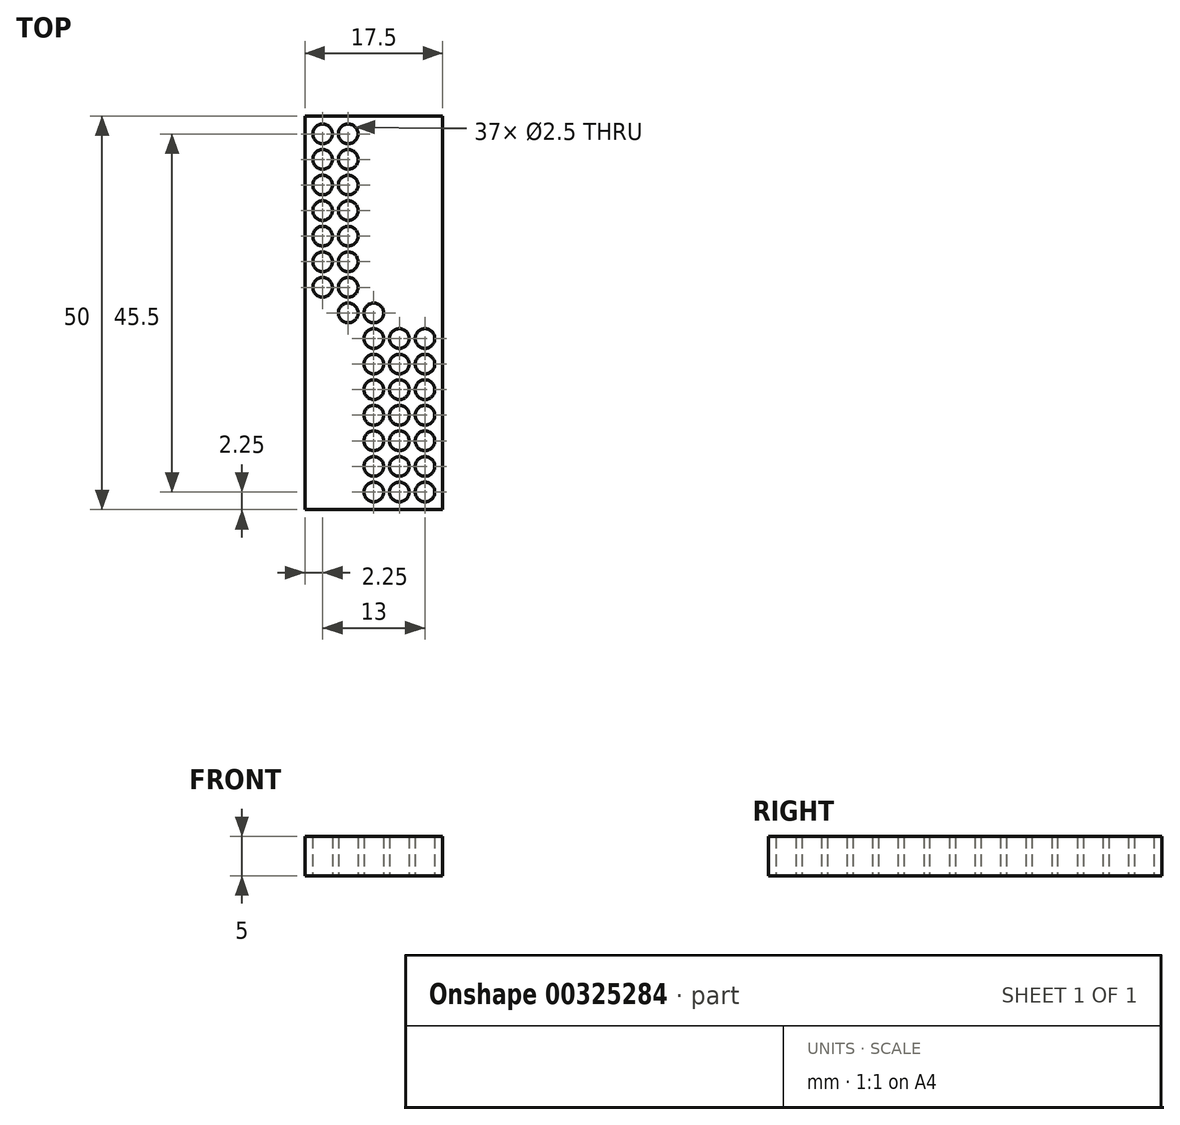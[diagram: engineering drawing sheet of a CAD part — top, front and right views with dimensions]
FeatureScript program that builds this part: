
annotation { "Feature Type Name" : "Feature", "Feature Type Description" : "" }
export const myFeature = defineFeature(function(context is Context, id is Id, definition is map)
    precondition{}
    {
        {
            var Q0;
            Q0=qCreatedBy(makeId("Top.planeOp"),FACE);
            var sketch = newSketch(context, id + "F0", { "sketchPlane" : qUnion([Q0])});
            skLineSegment(sketch, "E0.bottom", {"start": v(8.75, -25) * mm, "end": v(-8.75, -25) * mm});
            skLineSegment(sketch, "E0.top", {"start": v(8.75, 25) * mm, "end": v(-8.75, 25) * mm});
            skLineSegment(sketch, "E0.left", {"start": v(8.75, -25) * mm, "end": v(8.75, 25) * mm});
            skLineSegment(sketch, "E0.right", {"start": v(-8.75, -25) * mm, "end": v(-8.75, 25) * mm});
            skPoint(sketch, "E0.middle", {"position": v(0, 0) * mm});
            skCircle(sketch, "E1", {"center": v(0, 0) * mm, "radius": 1.25 * mm});
            skCircle(sketch, "E2.0.1.0", {"center": v(0, 3.25) * mm, "radius": 1.25 * mm});
            skCircle(sketch, "E2.0.2.0", {"center": v(0, 6.5) * mm, "radius": 1.25 * mm});
            skCircle(sketch, "E2.0.3.0", {"center": v(0, 9.75) * mm, "radius": 1.25 * mm});
            skCircle(sketch, "E2.0.4.0", {"center": v(0, 13) * mm, "radius": 1.25 * mm});
            skCircle(sketch, "E2.0.5.0", {"center": v(0, 16.25) * mm, "radius": 1.25 * mm});
            skCircle(sketch, "E2.0.6.0", {"center": v(0, 19.5) * mm, "radius": 1.25 * mm});
            skCircle(sketch, "E2.0.7.0", {"center": v(0, 22.75) * mm, "radius": 1.25 * mm});
            skCircle(sketch, "E2.1.0.0", {"center": v(3.25, 0) * mm, "radius": 1.25 * mm});
            skCircle(sketch, "E2.1.1.0", {"center": v(3.25, 3.25) * mm, "radius": 1.25 * mm});
            skCircle(sketch, "E2.1.2.0", {"center": v(3.25, 6.5) * mm, "radius": 1.25 * mm});
            skCircle(sketch, "E2.1.3.0", {"center": v(3.25, 9.75) * mm, "radius": 1.25 * mm});
            skCircle(sketch, "E2.1.4.0", {"center": v(3.25, 13) * mm, "radius": 1.25 * mm});
            skCircle(sketch, "E2.1.5.0", {"center": v(3.25, 16.25) * mm, "radius": 1.25 * mm});
            skCircle(sketch, "E2.1.6.0", {"center": v(3.25, 19.5) * mm, "radius": 1.25 * mm});
            skCircle(sketch, "E2.1.7.0", {"center": v(3.25, 22.75) * mm, "radius": 1.25 * mm});
            skCircle(sketch, "E2.2.0.0", {"center": v(6.5, 0) * mm, "radius": 1.25 * mm});
            skCircle(sketch, "E2.2.1.0", {"center": v(6.5, 3.25) * mm, "radius": 1.25 * mm});
            skCircle(sketch, "E2.2.2.0", {"center": v(6.5, 6.5) * mm, "radius": 1.25 * mm});
            skCircle(sketch, "E2.2.3.0", {"center": v(6.5, 9.75) * mm, "radius": 1.25 * mm});
            skCircle(sketch, "E2.2.4.0", {"center": v(6.5, 13) * mm, "radius": 1.25 * mm});
            skCircle(sketch, "E2.2.5.0", {"center": v(6.5, 16.25) * mm, "radius": 1.25 * mm});
            skCircle(sketch, "E2.2.6.0", {"center": v(6.5, 19.5) * mm, "radius": 1.25 * mm});
            skCircle(sketch, "E2.2.7.0", {"center": v(6.5, 22.75) * mm, "radius": 1.25 * mm});
            skLineSegment(sketch, "E2.direction1", {"start": v(0, 0) * mm, "end": v(3.25, 0) * mm, "construction": true});
            skLineSegment(sketch, "E2.direction2", {"start": v(0, 0) * mm, "end": v(0, 3.25) * mm, "construction": true});
            skCircle(sketch, "E3.MirrorC", {"center": v(-3.25, 19.5) * mm, "radius": 1.25 * mm});
            skCircle(sketch, "E4.MirrorC", {"center": v(-6.5, 9.75) * mm, "radius": 1.25 * mm});
            skCircle(sketch, "E5.MirrorC", {"center": v(-6.5, 6.5) * mm, "radius": 1.25 * mm});
            skCircle(sketch, "E6.MirrorC", {"center": v(-6.5, 16.25) * mm, "radius": 1.25 * mm});
            skCircle(sketch, "E7.MirrorC", {"center": v(-6.5, 3.25) * mm, "radius": 1.25 * mm});
            skCircle(sketch, "E8.MirrorC", {"center": v(-6.5, 22.75) * mm, "radius": 1.25 * mm});
            skCircle(sketch, "E9.MirrorC", {"center": v(-6.5, 13) * mm, "radius": 1.25 * mm});
            skCircle(sketch, "E10.MirrorC", {"center": v(-3.25, 13) * mm, "radius": 1.25 * mm});
            skCircle(sketch, "E11.MirrorC", {"center": v(-3.25, 9.75) * mm, "radius": 1.25 * mm});
            skCircle(sketch, "E12.MirrorC", {"center": v(-3.25, 6.5) * mm, "radius": 1.25 * mm});
            skCircle(sketch, "E13.MirrorC", {"center": v(-3.25, 16.25) * mm, "radius": 1.25 * mm});
            skCircle(sketch, "E14.MirrorC", {"center": v(-3.25, 3.25) * mm, "radius": 1.25 * mm});
            skCircle(sketch, "E15.MirrorC", {"center": v(-3.25, 22.75) * mm, "radius": 1.25 * mm});
            skCircle(sketch, "E16.MirrorC", {"center": v(-6.5, 19.5) * mm, "radius": 1.25 * mm});
            skCircle(sketch, "E17.MirrorC", {"center": v(-3.25, -22.75) * mm, "radius": 1.25 * mm});
            skCircle(sketch, "E18.MirrorC", {"center": v(-3.25, -19.5) * mm, "radius": 1.25 * mm});
            skCircle(sketch, "E19.MirrorC", {"center": v(-3.25, -9.75) * mm, "radius": 1.25 * mm});
            skCircle(sketch, "E20.MirrorC", {"center": v(-6.5, -16.25) * mm, "radius": 1.25 * mm});
            skCircle(sketch, "E21.MirrorC", {"center": v(-3.25, -6.5) * mm, "radius": 1.25 * mm});
            skCircle(sketch, "E22.MirrorC", {"center": v(-3.25, -16.25) * mm, "radius": 1.25 * mm});
            skCircle(sketch, "E23.MirrorC", {"center": v(-3.25, -3.25) * mm, "radius": 1.25 * mm});
            skCircle(sketch, "E24.MirrorC", {"center": v(-6.5, -9.75) * mm, "radius": 1.25 * mm});
            skCircle(sketch, "E25.MirrorC", {"center": v(-6.5, -19.5) * mm, "radius": 1.25 * mm});
            skCircle(sketch, "E26.MirrorC", {"center": v(-6.5, -22.75) * mm, "radius": 1.25 * mm});
            skCircle(sketch, "E27.MirrorC", {"center": v(-6.5, -13) * mm, "radius": 1.25 * mm});
            skCircle(sketch, "E28.MirrorC", {"center": v(-6.5, -6.5) * mm, "radius": 1.25 * mm});
            skCircle(sketch, "E29.MirrorC", {"center": v(-6.5, -3.25) * mm, "radius": 1.25 * mm});
            skCircle(sketch, "E30.MirrorC", {"center": v(-3.25, -13) * mm, "radius": 1.25 * mm});
            skCircle(sketch, "E31.MirrorC", {"center": v(3.25, -13) * mm, "radius": 1.25 * mm});
            skCircle(sketch, "E32.MirrorC", {"center": v(3.25, -9.75) * mm, "radius": 1.25 * mm});
            skCircle(sketch, "E33.MirrorC", {"center": v(6.5, -16.25) * mm, "radius": 1.25 * mm});
            skCircle(sketch, "E34.MirrorC", {"center": v(3.25, -6.5) * mm, "radius": 1.25 * mm});
            skCircle(sketch, "E35.MirrorC", {"center": v(3.25, -3.25) * mm, "radius": 1.25 * mm});
            skCircle(sketch, "E36.MirrorC", {"center": v(3.25, -22.75) * mm, "radius": 1.25 * mm});
            skCircle(sketch, "E37.MirrorC", {"center": v(3.25, -19.5) * mm, "radius": 1.25 * mm});
            skCircle(sketch, "E38.MirrorC", {"center": v(6.5, -6.5) * mm, "radius": 1.25 * mm});
            skCircle(sketch, "E39.MirrorC", {"center": v(6.5, -19.5) * mm, "radius": 1.25 * mm});
            skCircle(sketch, "E40.MirrorC", {"center": v(6.5, -13) * mm, "radius": 1.25 * mm});
            skCircle(sketch, "E41.MirrorC", {"center": v(6.5, -3.25) * mm, "radius": 1.25 * mm});
            skCircle(sketch, "E42.MirrorC", {"center": v(6.5, -22.75) * mm, "radius": 1.25 * mm});
            skCircle(sketch, "E43.MirrorC", {"center": v(3.25, -16.25) * mm, "radius": 1.25 * mm});
            skCircle(sketch, "E44.MirrorC", {"center": v(6.5, -9.75) * mm, "radius": 1.25 * mm});
            skCircle(sketch, "E45.MirrorC", {"center": v(0, -6.5) * mm, "radius": 1.25 * mm});
            skCircle(sketch, "E46.MirrorC", {"center": v(0, -9.75) * mm, "radius": 1.25 * mm});
            skCircle(sketch, "E47.MirrorC", {"center": v(0, -22.75) * mm, "radius": 1.25 * mm});
            skCircle(sketch, "E48.MirrorC", {"center": v(0, -19.5) * mm, "radius": 1.25 * mm});
            skCircle(sketch, "E49.MirrorC", {"center": v(0, -16.25) * mm, "radius": 1.25 * mm});
            skCircle(sketch, "E50.MirrorC", {"center": v(0, -13) * mm, "radius": 1.25 * mm});
            skCircle(sketch, "E51.MirrorC", {"center": v(0, -3.25) * mm, "radius": 1.25 * mm});
            skLineSegment(sketch, "E52.MirrorCS", {"start": v(8.75, 25) * mm, "end": v(8.75, -25) * mm});
            skCircle(sketch, "E53.MirrorC", {"center": v(-6.5, 0) * mm, "radius": 1.25 * mm});
            skCircle(sketch, "E54.MirrorC", {"center": v(-3.25, 0) * mm, "radius": 1.25 * mm});
            skSolve(sketch);
        }
        {
            var Q0;
            Q0=makeQuery(id+"F0.imprint","IMPRINT",FACE,{"disambiguationData":[TD([[makeQuery(id+"F0.imprint","IMPRINT",EDGE,{"derivedFrom":sQuery(id+"F0.wireOp",EDGE,"E0.bottom")}),-1.0]])]});
            extrude(context, id + "F1", {"entities" : qUnion([Q0]), "depth" : 1 * mm});
        }
        {
            var Q0;
            Q0=makeQuery(id+"F0.imprint","IMPRINT",FACE,{"disambiguationData":[TD([[makeQuery(id+"F0.imprint","IMPRINT",EDGE,{"derivedFrom":sQuery(id+"F0.wireOp",EDGE,"E8.MirrorC")}),-1.0]])]});
            var Q1;
            Q1=makeQuery(id+"F0.imprint","IMPRINT",FACE,{"disambiguationData":[TD([[makeQuery(id+"F0.imprint","IMPRINT",EDGE,{"derivedFrom":sQuery(id+"F0.wireOp",EDGE,"E15.MirrorC")}),-1.0]])]});
            var Q2;
            Q2=makeQuery(id+"F0.imprint","IMPRINT",FACE,{"disambiguationData":[TD([[makeQuery(id+"F0.imprint","IMPRINT",EDGE,{"derivedFrom":sQuery(id+"F0.wireOp",EDGE,"E2.0.7.0")}),1.0]])]});
            var Q3;
            Q3=makeQuery(id+"F0.imprint","IMPRINT",FACE,{"disambiguationData":[TD([[makeQuery(id+"F0.imprint","IMPRINT",EDGE,{"derivedFrom":sQuery(id+"F0.wireOp",EDGE,"E2.1.7.0")}),1.0]])]});
            var Q4;
            Q4=makeQuery(id+"F0.imprint","IMPRINT",FACE,{"disambiguationData":[TD([[makeQuery(id+"F0.imprint","IMPRINT",EDGE,{"derivedFrom":sQuery(id+"F0.wireOp",EDGE,"E2.2.7.0")}),1.0]])]});
            var Q5;
            Q5=makeQuery(id+"F0.imprint","IMPRINT",FACE,{"disambiguationData":[TD([[makeQuery(id+"F0.imprint","IMPRINT",EDGE,{"derivedFrom":sQuery(id+"F0.wireOp",EDGE,"E2.2.6.0")}),1.0]])]});
            var Q6;
            Q6=makeQuery(id+"F0.imprint","IMPRINT",FACE,{"disambiguationData":[TD([[makeQuery(id+"F0.imprint","IMPRINT",EDGE,{"derivedFrom":sQuery(id+"F0.wireOp",EDGE,"E2.2.5.0")}),1.0]])]});
            var Q7;
            Q7=makeQuery(id+"F0.imprint","IMPRINT",FACE,{"disambiguationData":[TD([[makeQuery(id+"F0.imprint","IMPRINT",EDGE,{"derivedFrom":sQuery(id+"F0.wireOp",EDGE,"E2.1.6.0")}),1.0]])]});
            var Q8;
            Q8=makeQuery(id+"F0.imprint","IMPRINT",FACE,{"disambiguationData":[TD([[makeQuery(id+"F0.imprint","IMPRINT",EDGE,{"derivedFrom":sQuery(id+"F0.wireOp",EDGE,"E2.1.5.0")}),1.0]])]});
            var Q9;
            Q9=makeQuery(id+"F0.imprint","IMPRINT",FACE,{"disambiguationData":[TD([[makeQuery(id+"F0.imprint","IMPRINT",EDGE,{"derivedFrom":sQuery(id+"F0.wireOp",EDGE,"E2.0.5.0")}),1.0]])]});
            var Q10;
            Q10=makeQuery(id+"F0.imprint","IMPRINT",FACE,{"disambiguationData":[TD([[makeQuery(id+"F0.imprint","IMPRINT",EDGE,{"derivedFrom":sQuery(id+"F0.wireOp",EDGE,"E2.0.6.0")}),1.0]])]});
            var Q11;
            Q11=makeQuery(id+"F0.imprint","IMPRINT",FACE,{"disambiguationData":[TD([[makeQuery(id+"F0.imprint","IMPRINT",EDGE,{"derivedFrom":sQuery(id+"F0.wireOp",EDGE,"E3.MirrorC")}),-1.0]])]});
            var Q12;
            Q12=makeQuery(id+"F0.imprint","IMPRINT",FACE,{"disambiguationData":[TD([[makeQuery(id+"F0.imprint","IMPRINT",EDGE,{"derivedFrom":sQuery(id+"F0.wireOp",EDGE,"E16.MirrorC")}),-1.0]])]});
            var Q13;
            Q13=makeQuery(id+"F0.imprint","IMPRINT",FACE,{"disambiguationData":[TD([[makeQuery(id+"F0.imprint","IMPRINT",EDGE,{"derivedFrom":sQuery(id+"F0.wireOp",EDGE,"E6.MirrorC")}),-1.0]])]});
            var Q14;
            Q14=makeQuery(id+"F0.imprint","IMPRINT",FACE,{"disambiguationData":[TD([[makeQuery(id+"F0.imprint","IMPRINT",EDGE,{"derivedFrom":sQuery(id+"F0.wireOp",EDGE,"E13.MirrorC")}),-1.0]])]});
            var Q15;
            Q15=makeQuery(id+"F0.imprint","IMPRINT",FACE,{"disambiguationData":[TD([[makeQuery(id+"F0.imprint","IMPRINT",EDGE,{"derivedFrom":sQuery(id+"F0.wireOp",EDGE,"E9.MirrorC")}),-1.0]])]});
            var Q16;
            Q16=makeQuery(id+"F0.imprint","IMPRINT",FACE,{"disambiguationData":[TD([[makeQuery(id+"F0.imprint","IMPRINT",EDGE,{"derivedFrom":sQuery(id+"F0.wireOp",EDGE,"E10.MirrorC")}),-1.0]])]});
            var Q17;
            Q17=makeQuery(id+"F0.imprint","IMPRINT",FACE,{"disambiguationData":[TD([[makeQuery(id+"F0.imprint","IMPRINT",EDGE,{"derivedFrom":sQuery(id+"F0.wireOp",EDGE,"E2.0.4.0")}),1.0]])]});
            var Q18;
            Q18=makeQuery(id+"F0.imprint","IMPRINT",FACE,{"disambiguationData":[TD([[makeQuery(id+"F0.imprint","IMPRINT",EDGE,{"derivedFrom":sQuery(id+"F0.wireOp",EDGE,"E2.1.4.0")}),1.0]])]});
            var Q19;
            Q19=makeQuery(id+"F0.imprint","IMPRINT",FACE,{"disambiguationData":[TD([[makeQuery(id+"F0.imprint","IMPRINT",EDGE,{"derivedFrom":sQuery(id+"F0.wireOp",EDGE,"E2.2.4.0")}),1.0]])]});
            var Q20;
            Q20=makeQuery(id+"F0.imprint","IMPRINT",FACE,{"disambiguationData":[TD([[makeQuery(id+"F0.imprint","IMPRINT",EDGE,{"derivedFrom":sQuery(id+"F0.wireOp",EDGE,"E2.2.3.0")}),1.0]])]});
            var Q21;
            Q21=makeQuery(id+"F0.imprint","IMPRINT",FACE,{"disambiguationData":[TD([[makeQuery(id+"F0.imprint","IMPRINT",EDGE,{"derivedFrom":sQuery(id+"F0.wireOp",EDGE,"E2.1.3.0")}),1.0]])]});
            var Q22;
            Q22=makeQuery(id+"F0.imprint","IMPRINT",FACE,{"disambiguationData":[TD([[makeQuery(id+"F0.imprint","IMPRINT",EDGE,{"derivedFrom":sQuery(id+"F0.wireOp",EDGE,"E2.0.3.0")}),1.0]])]});
            var Q23;
            Q23=makeQuery(id+"F0.imprint","IMPRINT",FACE,{"disambiguationData":[TD([[makeQuery(id+"F0.imprint","IMPRINT",EDGE,{"derivedFrom":sQuery(id+"F0.wireOp",EDGE,"E11.MirrorC")}),-1.0]])]});
            var Q24;
            Q24=makeQuery(id+"F0.imprint","IMPRINT",FACE,{"disambiguationData":[TD([[makeQuery(id+"F0.imprint","IMPRINT",EDGE,{"derivedFrom":sQuery(id+"F0.wireOp",EDGE,"E4.MirrorC")}),-1.0]])]});
            var Q25;
            Q25=makeQuery(id+"F0.imprint","IMPRINT",FACE,{"disambiguationData":[TD([[makeQuery(id+"F0.imprint","IMPRINT",EDGE,{"derivedFrom":sQuery(id+"F0.wireOp",EDGE,"E5.MirrorC")}),-1.0]])]});
            var Q26;
            Q26=makeQuery(id+"F0.imprint","IMPRINT",FACE,{"disambiguationData":[TD([[makeQuery(id+"F0.imprint","IMPRINT",EDGE,{"derivedFrom":sQuery(id+"F0.wireOp",EDGE,"E12.MirrorC")}),-1.0]])]});
            var Q27;
            Q27=makeQuery(id+"F0.imprint","IMPRINT",FACE,{"disambiguationData":[TD([[makeQuery(id+"F0.imprint","IMPRINT",EDGE,{"derivedFrom":sQuery(id+"F0.wireOp",EDGE,"E2.0.2.0")}),1.0]])]});
            var Q28;
            Q28=makeQuery(id+"F0.imprint","IMPRINT",FACE,{"disambiguationData":[TD([[makeQuery(id+"F0.imprint","IMPRINT",EDGE,{"derivedFrom":sQuery(id+"F0.wireOp",EDGE,"E2.1.2.0")}),1.0]])]});
            var Q29;
            Q29=makeQuery(id+"F0.imprint","IMPRINT",FACE,{"disambiguationData":[TD([[makeQuery(id+"F0.imprint","IMPRINT",EDGE,{"derivedFrom":sQuery(id+"F0.wireOp",EDGE,"E2.2.2.0")}),1.0]])]});
            var Q30;
            Q30=makeQuery(id+"F0.imprint","IMPRINT",FACE,{"disambiguationData":[TD([[makeQuery(id+"F0.imprint","IMPRINT",EDGE,{"derivedFrom":sQuery(id+"F0.wireOp",EDGE,"E2.2.1.0")}),1.0]])]});
            var Q31;
            Q31=makeQuery(id+"F0.imprint","IMPRINT",FACE,{"disambiguationData":[TD([[makeQuery(id+"F0.imprint","IMPRINT",EDGE,{"derivedFrom":sQuery(id+"F0.wireOp",EDGE,"E2.1.1.0")}),1.0]])]});
            var Q32;
            Q32=makeQuery(id+"F0.imprint","IMPRINT",FACE,{"disambiguationData":[TD([[makeQuery(id+"F0.imprint","IMPRINT",EDGE,{"derivedFrom":sQuery(id+"F0.wireOp",EDGE,"E2.0.1.0")}),1.0]])]});
            var Q33;
            Q33=makeQuery(id+"F0.imprint","IMPRINT",FACE,{"disambiguationData":[TD([[makeQuery(id+"F0.imprint","IMPRINT",EDGE,{"derivedFrom":sQuery(id+"F0.wireOp",EDGE,"E14.MirrorC")}),-1.0]])]});
            var Q34;
            Q34=makeQuery(id+"F0.imprint","IMPRINT",FACE,{"disambiguationData":[TD([[makeQuery(id+"F0.imprint","IMPRINT",EDGE,{"derivedFrom":sQuery(id+"F0.wireOp",EDGE,"E7.MirrorC")}),-1.0]])]});
            var Q35;
            Q35=makeQuery(id+"F0.imprint","IMPRINT",FACE,{"disambiguationData":[TD([[makeQuery(id+"F0.imprint","IMPRINT",EDGE,{"derivedFrom":sQuery(id+"F0.wireOp",EDGE,"E53.MirrorC")}),1.0]])]});
            var Q36;
            Q36=makeQuery(id+"F0.imprint","IMPRINT",FACE,{"disambiguationData":[TD([[makeQuery(id+"F0.imprint","IMPRINT",EDGE,{"derivedFrom":sQuery(id+"F0.wireOp",EDGE,"E54.MirrorC")}),-1.0]])]});
            var Q37;
            Q37=makeQuery(id+"F0.imprint","IMPRINT",FACE,{"disambiguationData":[TD([[makeQuery(id+"F0.imprint","IMPRINT",EDGE,{"derivedFrom":sQuery(id+"F0.wireOp",EDGE,"E1")}),-1.0]])]});
            var Q38;
            Q38=makeQuery(id+"F0.imprint","IMPRINT",FACE,{"disambiguationData":[TD([[makeQuery(id+"F0.imprint","IMPRINT",EDGE,{"derivedFrom":sQuery(id+"F0.wireOp",EDGE,"E2.1.0.0")}),1.0]])]});
            var Q39;
            Q39=makeQuery(id+"F0.imprint","IMPRINT",FACE,{"disambiguationData":[TD([[makeQuery(id+"F0.imprint","IMPRINT",EDGE,{"derivedFrom":sQuery(id+"F0.wireOp",EDGE,"E2.2.0.0")}),1.0]])]});
            var Q40;
            Q40=makeQuery(id+"F0.imprint","IMPRINT",FACE,{"disambiguationData":[TD([[makeQuery(id+"F0.imprint","IMPRINT",EDGE,{"derivedFrom":sQuery(id+"F0.wireOp",EDGE,"E41.MirrorC")}),-1.0]])]});
            var Q41;
            Q41=makeQuery(id+"F0.imprint","IMPRINT",FACE,{"disambiguationData":[TD([[makeQuery(id+"F0.imprint","IMPRINT",EDGE,{"derivedFrom":sQuery(id+"F0.wireOp",EDGE,"E35.MirrorC")}),-1.0]])]});
            var Q42;
            Q42=makeQuery(id+"F0.imprint","IMPRINT",FACE,{"disambiguationData":[TD([[makeQuery(id+"F0.imprint","IMPRINT",EDGE,{"derivedFrom":sQuery(id+"F0.wireOp",EDGE,"E51.MirrorC")}),-1.0]])]});
            var Q43;
            Q43=makeQuery(id+"F0.imprint","IMPRINT",FACE,{"disambiguationData":[TD([[makeQuery(id+"F0.imprint","IMPRINT",EDGE,{"derivedFrom":sQuery(id+"F0.wireOp",EDGE,"E23.MirrorC")}),1.0]])]});
            var Q44;
            Q44=makeQuery(id+"F0.imprint","IMPRINT",FACE,{"disambiguationData":[TD([[makeQuery(id+"F0.imprint","IMPRINT",EDGE,{"derivedFrom":sQuery(id+"F0.wireOp",EDGE,"E29.MirrorC")}),1.0]])]});
            var Q45;
            Q45=makeQuery(id+"F0.imprint","IMPRINT",FACE,{"disambiguationData":[TD([[makeQuery(id+"F0.imprint","IMPRINT",EDGE,{"derivedFrom":sQuery(id+"F0.wireOp",EDGE,"E28.MirrorC")}),1.0]])]});
            var Q46;
            Q46=makeQuery(id+"F0.imprint","IMPRINT",FACE,{"disambiguationData":[TD([[makeQuery(id+"F0.imprint","IMPRINT",EDGE,{"derivedFrom":sQuery(id+"F0.wireOp",EDGE,"E21.MirrorC")}),1.0]])]});
            var Q47;
            Q47=makeQuery(id+"F0.imprint","IMPRINT",FACE,{"disambiguationData":[TD([[makeQuery(id+"F0.imprint","IMPRINT",EDGE,{"derivedFrom":sQuery(id+"F0.wireOp",EDGE,"E45.MirrorC")}),-1.0]])]});
            var Q48;
            Q48=makeQuery(id+"F0.imprint","IMPRINT",FACE,{"disambiguationData":[TD([[makeQuery(id+"F0.imprint","IMPRINT",EDGE,{"derivedFrom":sQuery(id+"F0.wireOp",EDGE,"E34.MirrorC")}),-1.0]])]});
            var Q49;
            Q49=makeQuery(id+"F0.imprint","IMPRINT",FACE,{"disambiguationData":[TD([[makeQuery(id+"F0.imprint","IMPRINT",EDGE,{"derivedFrom":sQuery(id+"F0.wireOp",EDGE,"E38.MirrorC")}),-1.0]])]});
            var Q50;
            Q50=makeQuery(id+"F0.imprint","IMPRINT",FACE,{"disambiguationData":[TD([[makeQuery(id+"F0.imprint","IMPRINT",EDGE,{"derivedFrom":sQuery(id+"F0.wireOp",EDGE,"E44.MirrorC")}),-1.0]])]});
            var Q51;
            Q51=makeQuery(id+"F0.imprint","IMPRINT",FACE,{"disambiguationData":[TD([[makeQuery(id+"F0.imprint","IMPRINT",EDGE,{"derivedFrom":sQuery(id+"F0.wireOp",EDGE,"E40.MirrorC")}),-1.0]])]});
            var Q52;
            Q52=makeQuery(id+"F0.imprint","IMPRINT",FACE,{"disambiguationData":[TD([[makeQuery(id+"F0.imprint","IMPRINT",EDGE,{"derivedFrom":sQuery(id+"F0.wireOp",EDGE,"E32.MirrorC")}),-1.0]])]});
            var Q53;
            Q53=makeQuery(id+"F0.imprint","IMPRINT",FACE,{"disambiguationData":[TD([[makeQuery(id+"F0.imprint","IMPRINT",EDGE,{"derivedFrom":sQuery(id+"F0.wireOp",EDGE,"E31.MirrorC")}),-1.0]])]});
            var Q54;
            Q54=makeQuery(id+"F0.imprint","IMPRINT",FACE,{"disambiguationData":[TD([[makeQuery(id+"F0.imprint","IMPRINT",EDGE,{"derivedFrom":sQuery(id+"F0.wireOp",EDGE,"E46.MirrorC")}),-1.0]])]});
            var Q55;
            Q55=makeQuery(id+"F0.imprint","IMPRINT",FACE,{"disambiguationData":[TD([[makeQuery(id+"F0.imprint","IMPRINT",EDGE,{"derivedFrom":sQuery(id+"F0.wireOp",EDGE,"E50.MirrorC")}),-1.0]])]});
            var Q56;
            Q56=makeQuery(id+"F0.imprint","IMPRINT",FACE,{"disambiguationData":[TD([[makeQuery(id+"F0.imprint","IMPRINT",EDGE,{"derivedFrom":sQuery(id+"F0.wireOp",EDGE,"E19.MirrorC")}),1.0]])]});
            var Q57;
            Q57=makeQuery(id+"F0.imprint","IMPRINT",FACE,{"disambiguationData":[TD([[makeQuery(id+"F0.imprint","IMPRINT",EDGE,{"derivedFrom":sQuery(id+"F0.wireOp",EDGE,"E30.MirrorC")}),1.0]])]});
            var Q58;
            Q58=makeQuery(id+"F0.imprint","IMPRINT",FACE,{"disambiguationData":[TD([[makeQuery(id+"F0.imprint","IMPRINT",EDGE,{"derivedFrom":sQuery(id+"F0.wireOp",EDGE,"E24.MirrorC")}),1.0]])]});
            var Q59;
            Q59=makeQuery(id+"F0.imprint","IMPRINT",FACE,{"disambiguationData":[TD([[makeQuery(id+"F0.imprint","IMPRINT",EDGE,{"derivedFrom":sQuery(id+"F0.wireOp",EDGE,"E27.MirrorC")}),1.0]])]});
            var Q60;
            Q60=makeQuery(id+"F0.imprint","IMPRINT",FACE,{"disambiguationData":[TD([[makeQuery(id+"F0.imprint","IMPRINT",EDGE,{"derivedFrom":sQuery(id+"F0.wireOp",EDGE,"E20.MirrorC")}),1.0]])]});
            var Q61;
            Q61=makeQuery(id+"F0.imprint","IMPRINT",FACE,{"disambiguationData":[TD([[makeQuery(id+"F0.imprint","IMPRINT",EDGE,{"derivedFrom":sQuery(id+"F0.wireOp",EDGE,"E25.MirrorC")}),1.0]])]});
            var Q62;
            Q62=makeQuery(id+"F0.imprint","IMPRINT",FACE,{"disambiguationData":[TD([[makeQuery(id+"F0.imprint","IMPRINT",EDGE,{"derivedFrom":sQuery(id+"F0.wireOp",EDGE,"E26.MirrorC")}),1.0]])]});
            var Q63;
            Q63=makeQuery(id+"F0.imprint","IMPRINT",FACE,{"disambiguationData":[TD([[makeQuery(id+"F0.imprint","IMPRINT",EDGE,{"derivedFrom":sQuery(id+"F0.wireOp",EDGE,"E17.MirrorC")}),1.0]])]});
            var Q64;
            Q64=makeQuery(id+"F0.imprint","IMPRINT",FACE,{"disambiguationData":[TD([[makeQuery(id+"F0.imprint","IMPRINT",EDGE,{"derivedFrom":sQuery(id+"F0.wireOp",EDGE,"E18.MirrorC")}),1.0]])]});
            var Q65;
            Q65=makeQuery(id+"F0.imprint","IMPRINT",FACE,{"disambiguationData":[TD([[makeQuery(id+"F0.imprint","IMPRINT",EDGE,{"derivedFrom":sQuery(id+"F0.wireOp",EDGE,"E22.MirrorC")}),1.0]])]});
            var Q66;
            Q66=makeQuery(id+"F0.imprint","IMPRINT",FACE,{"disambiguationData":[TD([[makeQuery(id+"F0.imprint","IMPRINT",EDGE,{"derivedFrom":sQuery(id+"F0.wireOp",EDGE,"E49.MirrorC")}),-1.0]])]});
            var Q67;
            Q67=makeQuery(id+"F0.imprint","IMPRINT",FACE,{"disambiguationData":[TD([[makeQuery(id+"F0.imprint","IMPRINT",EDGE,{"derivedFrom":sQuery(id+"F0.wireOp",EDGE,"E48.MirrorC")}),-1.0]])]});
            var Q68;
            Q68=makeQuery(id+"F0.imprint","IMPRINT",FACE,{"disambiguationData":[TD([[makeQuery(id+"F0.imprint","IMPRINT",EDGE,{"derivedFrom":sQuery(id+"F0.wireOp",EDGE,"E47.MirrorC")}),-1.0]])]});
            var Q69;
            Q69=makeQuery(id+"F0.imprint","IMPRINT",FACE,{"disambiguationData":[TD([[makeQuery(id+"F0.imprint","IMPRINT",EDGE,{"derivedFrom":sQuery(id+"F0.wireOp",EDGE,"E36.MirrorC")}),-1.0]])]});
            var Q70;
            Q70=makeQuery(id+"F0.imprint","IMPRINT",FACE,{"disambiguationData":[TD([[makeQuery(id+"F0.imprint","IMPRINT",EDGE,{"derivedFrom":sQuery(id+"F0.wireOp",EDGE,"E37.MirrorC")}),-1.0]])]});
            var Q71;
            Q71=makeQuery(id+"F0.imprint","IMPRINT",FACE,{"disambiguationData":[TD([[makeQuery(id+"F0.imprint","IMPRINT",EDGE,{"derivedFrom":sQuery(id+"F0.wireOp",EDGE,"E43.MirrorC")}),-1.0]])]});
            var Q72;
            Q72=makeQuery(id+"F0.imprint","IMPRINT",FACE,{"disambiguationData":[TD([[makeQuery(id+"F0.imprint","IMPRINT",EDGE,{"derivedFrom":sQuery(id+"F0.wireOp",EDGE,"E33.MirrorC")}),-1.0]])]});
            var Q73;
            Q73=makeQuery(id+"F0.imprint","IMPRINT",FACE,{"disambiguationData":[TD([[makeQuery(id+"F0.imprint","IMPRINT",EDGE,{"derivedFrom":sQuery(id+"F0.wireOp",EDGE,"E39.MirrorC")}),-1.0]])]});
            var Q74;
            Q74=makeQuery(id+"F0.imprint","IMPRINT",FACE,{"disambiguationData":[TD([[makeQuery(id+"F0.imprint","IMPRINT",EDGE,{"derivedFrom":sQuery(id+"F0.wireOp",EDGE,"E42.MirrorC")}),-1.0]])]});
            extrude(context, id + "F2", {"entities" : qUnion([Q0, Q1, Q2, Q3, Q4, Q5, Q6, Q7, Q8, Q9, Q10, Q11, Q12, Q13, Q14, Q15, Q16, Q17, Q18, Q19, Q20, Q21, Q22, Q23, Q24, Q25, Q26, Q27, Q28, Q29, Q30, Q31, Q32, Q33, Q34, Q35, Q36, Q37, Q38, Q39, Q40, Q41, Q42, Q43, Q44, Q45, Q46, Q47, Q48, Q49, Q50, Q51, Q52, Q53, Q54, Q55, Q56, Q57, Q58, Q59, Q60, Q61, Q62, Q63, Q64, Q65, Q66, Q67, Q68, Q69, Q70, Q71, Q72, Q73, Q74]), "operationType" : NewBodyOperationType.ADD, "depth" : 5 * mm});
        }
    });
